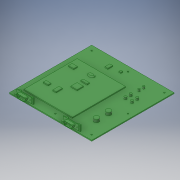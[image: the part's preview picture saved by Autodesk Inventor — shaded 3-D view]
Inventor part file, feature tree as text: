
AUTODESK INVENTOR PART (.ipt)
format: ipt  version: 2018 (Build 220112000, 112)  size: 468,480 bytes
history: native  units: in
note: dims shown in document units (in); Inventor stores cm internally (conversion verified against a paired STEP export)
features: sketch x13, extrude x12, projected_geometry x6, plane x2, fillet x1, hole x1
ambient origin geometry x8: Origin, YZ Plane, XZ Plane, XY Plane, X Axis, Y Axis, Z Axis, Center Point
bodies: Solid1 (feature_tree)
feature tree (35):
  extrude  "Extrusion1"  Depth=6.6929in
  sketch  "Sketch2"  dims[d2=0.0787in d3=0.0in d4=5.9055in]
  extrude  "Extrusion3"  Depth=0.0787in
  plane  "Work Plane1"
  extrude  "Extrusion4"  Depth=0.3937in
  extrude  "Extrusion5"  Depth=0.3937in
  extrude  "Extrusion6"  Depth=0.1969in
  extrude  "Extrusion7"  Depth=0.1969in
  plane  "Work Plane2"
  extrude  "Extrusion8"  Depth=2.7559in
  extrude  "Extrusion9"  Depth=2.7559in
  extrude  "Extrusion10"  Depth=0.9843in
  extrude  "Extrusion12"  TaperAngle=0.0deg  [1 undecoded]
  extrude  "Extrusion13"  Depth=0.1575in TaperAngle=0.0deg
  extrude  "Extrusion14"  Depth=0.0787in TaperAngle=0.0deg
  fillet  "Fillet1"  Radius=0.3937in
  hole  "Hole1"  [1 undecoded]
  sketch  "Sketch1"  dims[d0=6.6929in d1=6.6929in]
  sketch  "Sketch3"  dims[d5=5.9055in d6=0.3937in]
  sketch  "Sketch5"  dims[d7=0.3937in d8=0.1181in]
  projected_geometry  "Projected Loop1"
  sketch  "Sketch6"  dims[d9=1.1811in d11=2.9528in d12=1.1811in d14=2.9528in d19=0.1969in]
  sketch  "Sketch7"  dims[d20=0.1969in d21=0.1969in]
  sketch  "Sketch8"  dims[d22=0.1969in d23=2.7559in]
  sketch  "Sketch9"  dims[d24=3.5433in d25=2.7559in]
  sketch  "Sketch10"  dims[d26=1.1811in d27=0.9843in]
  sketch  "Sketch11"  dims[d28=0.0in d29=0.0in]
  projected_geometry  "Projected Loop2"
  sketch  "Sketch14"  dims[d30=3.5433in d31=0.1575in d32=0.0in]
  sketch  "Sketch15"  dims[d37=0.1575in d38=0.0787in d39=0.0in d40=0.3937in]
  projected_geometry  "Projected Loop3"
  projected_geometry  "Projected Loop4"
  projected_geometry  "Projected Loop5"
  projected_geometry  "Projected Loop6"
  sketch  "Sketch16"  dims[d41=0.3937in d42=0.2362in d43=0.0in d44=0.1969in d45=0.1969in d46=0.1969in d47=0.1969in d48=0.1575in d49=0.1575in d50=0.1575in d51=0.0in d52=0.2362in d53=0.3937in d54=0.1575in d55=0.1575in d56=0.0787in d57=0.0in d58=0.5906in d59=1.2598in d60=0.4331in d61=1.2598in d62=0.4331in d63=2.5591in d64=0.0394in d65=0.0in d66=0.0984in d67=0.0984in d68=0.9843in d69=0.2165in d70=0.2165in d71=0.1378in d74=0.0787in d78=0.0394in d79=0.0197in d80=0.0919in d81=0.7874in d83=0.0919in d84=3.1496in d86=0.0689in d89=0.0157in d91=0.7874in d93=3.1496in d94=0.0984in d95=0.0984in d96=0.9843in d97=0.0394in d98=0.0197in d99=0.0919in d100=0.0919in d101=0.0689in d102=0.0157in d103=0.1378in d104=0.2165in d105=0.2165in d106=0.2362in d107=0.0in d108=0.1575in d109=0.0in d112=0.1969in d113=0.1969in d114=0.0984in d115=0.0984in d116=0.1969in d117=0.1969in d118=0.1969in d119=0.1969in d120=0.1969in d121=0.1969in d122=0.0984in d123=0.0984in d124=0.0984in d125=0.0984in d126=0.0984in d127=0.0984in d128=0.0787in d129=0.0in d130=0.0787in d131=0.0in d132=0.3937in d133=0.2362in d134=0.5118in d135=0.5118in d136=0.1969in d137=0.4331in d138=0.315in d139=0.2756in d140=0.5118in d141=0.0787in d142=0.0in d143=0.0787in d144=0.1181in d145=0.2362in d146=0.1575in d147=0.0787in d148=90.0deg d149=0.315in d150=0.8108in]
note: 2 required parameter values undecoded (feature->parameter linkage not recoverable at this tier; creation-order binding heuristic only, values carry confidence <= 0.55)
